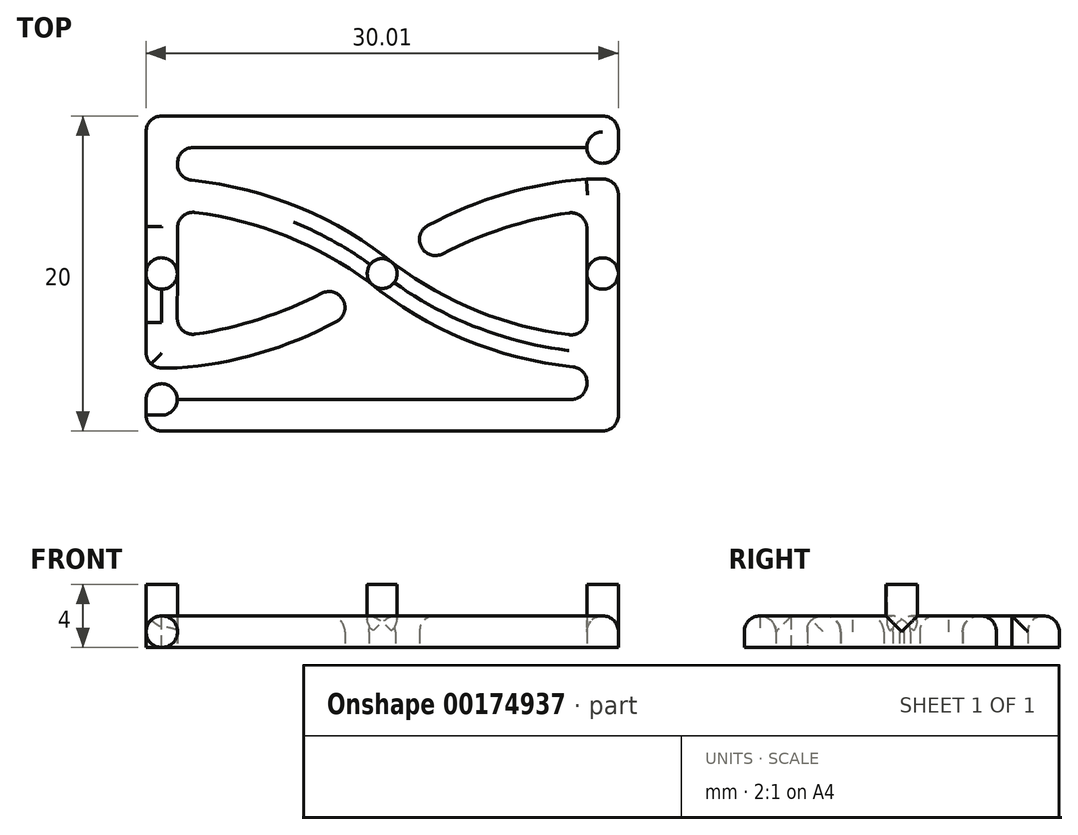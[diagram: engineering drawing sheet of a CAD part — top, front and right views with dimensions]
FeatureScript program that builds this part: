
annotation { "Feature Type Name" : "Feature", "Feature Type Description" : "" }
export const myFeature = defineFeature(function(context is Context, id is Id, definition is map)
    precondition{}
    {
        {
            var Q0;
            Q0=qCreatedBy(makeId("Top.planeOp"),FACE);
            var sketch = newSketch(context, id + "F0", { "sketchPlane" : qUnion([Q0])});
            skLineSegment(sketch, "E0", {"start": v(-15, 10) * mm, "end": v(-15, -6) * mm, "construction": true});
            skLineSegment(sketch, "E1", {"start": v(-15, -10) * mm, "end": v(15, -10) * mm, "construction": true});
            skLineSegment(sketch, "E2", {"start": v(15, -10) * mm, "end": v(15, 6.02) * mm, "construction": true});
            skLineSegment(sketch, "E3", {"start": v(15, 10) * mm, "end": v(-15, 10) * mm, "construction": true});
            skLineSegment(sketch, "E4", {"start": v(-15, 10) * mm, "end": v(15, 10) * mm});
            skLineSegment(sketch, "E5", {"start": v(15, 7) * mm, "end": v(13, 7) * mm});
            skLineSegment(sketch, "E6", {"start": v(13, 7) * mm, "end": v(13, 8) * mm});
            skLineSegment(sketch, "E7", {"start": v(13, 8) * mm, "end": v(-13, 8) * mm});
            skLineSegment(sketch, "E8", {"start": v(-13, 8) * mm, "end": v(-13, 6) * mm});
            skLineSegment(sketch, "E9", {"start": v(-15, 10) * mm, "end": v(-15, -7.49) * mm});
            skLineSegment(sketch, "E10", {"start": v(-15, -10) * mm, "end": v(-15, -7) * mm});
            skLineSegment(sketch, "E11", {"start": v(-15, -7) * mm, "end": v(-13.02, -7) * mm});
            skLineSegment(sketch, "E12", {"start": v(-13.02, -7) * mm, "end": v(-13.02, -8) * mm});
            skLineSegment(sketch, "E13", {"start": v(-13.02, -8) * mm, "end": v(13, -8) * mm});
            skLineSegment(sketch, "E14", {"start": v(13, -8) * mm, "end": v(13, -6) * mm});
            skLineSegment(sketch, "E15", {"start": v(-15, -7) * mm, "end": v(-15, -10) * mm});
            skLineSegment(sketch, "E16", {"start": v(15, -10) * mm, "end": v(-15, -10) * mm});
            skLineSegment(sketch, "E17", {"start": v(15, -10) * mm, "end": v(15, 7) * mm});
            skLineSegment(sketch, "E18", {"start": v(15, 10) * mm, "end": v(-15, -10) * mm, "construction": true});
            skLineSegment(sketch, "E19", {"start": v(-15, 10) * mm, "end": v(15, -10) * mm, "construction": true});
            skPoint(sketch, "E20", {"position": v(0, 0) * mm});
            skLineSegment(sketch, "E21", {"start": v(0, 0) * mm, "end": v(0.83, -0.55) * mm});
            skArc(sketch, "E22", {"start": v(0.83, 0.55) * mm, "mid": v(-5.66, 4.36) * mm, "end": v(-13, 6) * mm});
            skPoint(sketch, "E23", {"position": v(13, -4) * mm});
            skPoint(sketch, "E24", {"position": v(-13, 6) * mm});
            skPoint(sketch, "E25", {"position": v(-13, 4) * mm});
            skArc(sketch, "E26", {"start": v(-0.83, -0.55) * mm, "mid": v(-6.6, 2.57) * mm, "end": v(-13, 4) * mm});
            skArc(sketch, "E27", {"start": v(-0.83, -0.55) * mm, "mid": v(5.66, -4.35) * mm, "end": v(13, -6) * mm});
            skArc(sketch, "E28", {"start": v(0.83, 0.55) * mm, "mid": v(6.6, -2.59) * mm, "end": v(13, -4) * mm});
            skPoint(sketch, "E29", {"position": v(13, 6) * mm});
            skPoint(sketch, "E30", {"position": v(-13.02, -6) * mm});
            skPoint(sketch, "E31", {"position": v(2.5, 1.66) * mm});
            skPoint(sketch, "E32", {"position": v(-2.5, -1.66) * mm});
            skLineSegment(sketch, "E33", {"start": v(-2.5, -1.66) * mm, "end": v(-3.05, -0.83) * mm, "construction": true});
            skLineSegment(sketch, "E34", {"start": v(-2.5, -1.66) * mm, "end": v(-1.94, -2.5) * mm, "construction": true});
            skLineSegment(sketch, "E35", {"start": v(2.5, 1.66) * mm, "end": v(3.05, 0.83) * mm, "construction": true});
            skLineSegment(sketch, "E36", {"start": v(3.05, 0.83) * mm, "end": v(1.94, 2.5) * mm, "construction": true});
            skLineSegment(sketch, "E37", {"start": v(15, 6.02) * mm, "end": v(13, 6) * mm});
            skPoint(sketch, "E38", {"position": v(-13.02, -4) * mm});
            skLineSegment(sketch, "E39", {"start": v(-13.02, -6) * mm, "end": v(-15, -6) * mm});
            skArc(sketch, "E40", {"start": v(-13.02, -6) * mm, "mid": v(-7.27, -4.9) * mm, "end": v(-1.94, -2.5) * mm});
            skArc(sketch, "E41", {"start": v(-13.02, -4) * mm, "mid": v(-7.88, -2.92) * mm, "end": v(-3.05, -0.83) * mm});
            skLineSegment(sketch, "E42", {"start": v(-3.05, -0.83) * mm, "end": v(-1.94, -2.5) * mm});
            skLineSegment(sketch, "E43", {"start": v(-13.02, -4) * mm, "end": v(-13, 4) * mm});
            skArc(sketch, "E44", {"start": v(13, 6) * mm, "mid": v(7.26, 4.9) * mm, "end": v(1.94, 2.5) * mm});
            skPoint(sketch, "E45", {"position": v(13, 4) * mm});
            skArc(sketch, "E46", {"start": v(13, 4) * mm, "mid": v(7.87, 2.92) * mm, "end": v(3.05, 0.83) * mm});
            skLineSegment(sketch, "E47", {"start": v(13, 4) * mm, "end": v(13, -4) * mm});
            skLineSegment(sketch, "E48", {"start": v(3.05, 0.83) * mm, "end": v(1.94, 2.5) * mm});
            skLineSegment(sketch, "E49", {"start": v(15, 6.02) * mm, "end": v(15, -10) * mm});
            skLineSegment(sketch, "E50", {"start": v(15, 7) * mm, "end": v(15, 10) * mm});
            skLineSegment(sketch, "E51.trimOffspring", {"start": v(15, 7) * mm, "end": v(15, 10) * mm, "construction": true});
            skLineSegment(sketch, "E52.trimOffspring", {"start": v(-15, -7) * mm, "end": v(-15, -10) * mm, "construction": true});
            skSolve(sketch);
        }
        {
            var Q0;
            {var subQ5=sQuery(id+"F0.wireOp",EDGE,"E4");Q0=makeQuery(id+"F0.imprint","IMPRINT",FACE,{"disambiguationData":[TD([[makeQuery(id+"F0.imprint","IMPRINT",EDGE,{"derivedFrom":subQ5}),-1.0]])]});}
            extrude(context, id + "F1", {"entities" : qUnion([Q0]), "depth" : 2 * mm});
        }
        {
            var Q0;
            Q0=makeQuery(id+"F1.opExtrude","SWEPT_EDGE",EDGE,{"disambiguationData":[OSD([sQuery(id+"F0.wireOp",EDGE,"E44"),sQuery(id+"F0.wireOp",EDGE,"E48")])]});
            var Q1;
            Q1=makeQuery(id+"F1.opExtrude","SWEPT_EDGE",EDGE,{"disambiguationData":[OSD([sQuery(id+"F0.wireOp",EDGE,"E46"),sQuery(id+"F0.wireOp",EDGE,"E48")])]});
            var Q2;
            Q2=makeQuery(id+"F1.opExtrude","SWEPT_EDGE",EDGE,{"disambiguationData":[OSD([sQuery(id+"F0.wireOp",EDGE,"E5"),sQuery(id+"F0.wireOp",EDGE,"E6")])]});
            var Q3;
            Q3=makeQuery(id+"F1.opExtrude","SWEPT_EDGE",EDGE,{"disambiguationData":[OSD([sQuery(id+"F0.wireOp",EDGE,"E5"),sQuery(id+"F0.wireOp",EDGE,"E17"),sQuery(id+"F0.wireOp",EDGE,"E50")])]});
            var Q4;
            Q4=makeQuery(id+"F1.opExtrude","SWEPT_EDGE",EDGE,{"disambiguationData":[OSD([sQuery(id+"F0.wireOp",EDGE,"E9"),sQuery(id+"F0.wireOp",EDGE,"E39")])]});
            var Q5;
            Q5=makeQuery(id+"F1.opExtrude","SWEPT_EDGE",EDGE,{"disambiguationData":[OSD([sQuery(id+"F0.wireOp",EDGE,"E9"),sQuery(id+"F0.wireOp",EDGE,"E11"),sQuery(id+"F0.wireOp",EDGE,"E15")])]});
            var Q6;
            Q6=makeQuery(id+"F1.opExtrude","SWEPT_EDGE",EDGE,{"disambiguationData":[OSD([sQuery(id+"F0.wireOp",EDGE,"E15"),sQuery(id+"F0.wireOp",EDGE,"E16")])]});
            var Q7;
            Q7=makeQuery(id+"F1.opExtrude","SWEPT_EDGE",EDGE,{"disambiguationData":[OSD([sQuery(id+"F0.wireOp",EDGE,"E46"),sQuery(id+"F0.wireOp",EDGE,"E47")])]});
            var Q8;
            Q8=makeQuery(id+"F1.opExtrude","SWEPT_EDGE",EDGE,{"disambiguationData":[OSD([sQuery(id+"F0.wireOp",EDGE,"E14"),sQuery(id+"F0.wireOp",EDGE,"E27")])]});
            var Q9;
            Q9=makeQuery(id+"F1.opExtrude","SWEPT_EDGE",EDGE,{"disambiguationData":[OSD([sQuery(id+"F0.wireOp",EDGE,"E16"),sQuery(id+"F0.wireOp",EDGE,"E49")])]});
            var Q10;
            Q10=makeQuery(id+"F1.opExtrude","SWEPT_EDGE",EDGE,{"disambiguationData":[OSD([sQuery(id+"F0.wireOp",EDGE,"E7"),sQuery(id+"F0.wireOp",EDGE,"E8")])]});
            var Q11;
            Q11=makeQuery(id+"F1.opExtrude","SWEPT_EDGE",EDGE,{"disambiguationData":[OSD([sQuery(id+"F0.wireOp",EDGE,"E26"),sQuery(id+"F0.wireOp",EDGE,"E43")])]});
            var Q12;
            Q12=makeQuery(id+"F1.opExtrude","SWEPT_EDGE",EDGE,{"disambiguationData":[OSD([sQuery(id+"F0.wireOp",EDGE,"E40"),sQuery(id+"F0.wireOp",EDGE,"E42")])]});
            var Q13;
            Q13=makeQuery(id+"F1.opExtrude","SWEPT_EDGE",EDGE,{"disambiguationData":[OSD([sQuery(id+"F0.wireOp",EDGE,"E4"),sQuery(id+"F0.wireOp",EDGE,"E50")])]});
            var Q14;
            Q14=makeQuery(id+"F1.opExtrude","SWEPT_EDGE",EDGE,{"disambiguationData":[OSD([sQuery(id+"F0.wireOp",EDGE,"E13"),sQuery(id+"F0.wireOp",EDGE,"E14")])]});
            var Q15;
            Q15=makeQuery(id+"F1.opExtrude","SWEPT_EDGE",EDGE,{"disambiguationData":[OSD([sQuery(id+"F0.wireOp",EDGE,"E28"),sQuery(id+"F0.wireOp",EDGE,"E47")])]});
            var Q16;
            Q16=makeQuery(id+"F1.opExtrude","SWEPT_EDGE",EDGE,{"disambiguationData":[OSD([sQuery(id+"F0.wireOp",EDGE,"E4"),sQuery(id+"F0.wireOp",EDGE,"E9")])]});
            var Q17;
            Q17=makeQuery(id+"F1.opExtrude","SWEPT_EDGE",EDGE,{"disambiguationData":[OSD([sQuery(id+"F0.wireOp",EDGE,"E41"),sQuery(id+"F0.wireOp",EDGE,"E43")])]});
            var Q18;
            Q18=makeQuery(id+"F1.opExtrude","SWEPT_EDGE",EDGE,{"disambiguationData":[OSD([sQuery(id+"F0.wireOp",EDGE,"E8"),sQuery(id+"F0.wireOp",EDGE,"E22")])]});
            var Q19;
            Q19=makeQuery(id+"F1.opExtrude","SWEPT_EDGE",EDGE,{"disambiguationData":[OSD([sQuery(id+"F0.wireOp",EDGE,"E41"),sQuery(id+"F0.wireOp",EDGE,"E42")])]});
            var Q20;
            Q20=makeQuery(id+"F1.opExtrude","SWEPT_EDGE",EDGE,{"disambiguationData":[OSD([sQuery(id+"F0.wireOp",EDGE,"E11"),sQuery(id+"F0.wireOp",EDGE,"E12")])]});
            var Q21;
            Q21=makeQuery(id+"F1.opExtrude","SWEPT_EDGE",EDGE,{"disambiguationData":[OSD([sQuery(id+"F0.wireOp",EDGE,"E17"),sQuery(id+"F0.wireOp",EDGE,"E37"),sQuery(id+"F0.wireOp",EDGE,"E49")])]});
            fillet(context, id + "F2", {"entities" : qUnion([Q0, Q1, Q2, Q3, Q4, Q5, Q6, Q7, Q8, Q9, Q10, Q11, Q12, Q13, Q14, Q15, Q16, Q17, Q18, Q19, Q20, Q21]), "radius" : 1 * mm, "tangentPropagation" : true, "allowEdgeOverflow" : false});
        }
        {
            var Q0;
            Q0=makeQuery(id+"F1.opExtrude","CAP_EDGE",EDGE,{"disambiguationData":[OSD([sQuery(id+"F0.wireOp",EDGE,"E27")])],"isStart":false});
            var Q1;
            Q1=makeQuery(id+"F1.opExtrude","CAP_EDGE",EDGE,{"disambiguationData":[OSD([sQuery(id+"F0.wireOp",EDGE,"E40")])],"isStart":false});
            var Q2;
            Q2=makeQuery(id+"F1.opExtrude","CAP_EDGE",EDGE,{"disambiguationData":[OSD([sQuery(id+"F0.wireOp",EDGE,"E46")])],"isStart":false});
            var Q3;
            Q3=makeQuery(id+"F1.opExtrude","CAP_EDGE",EDGE,{"disambiguationData":[OSD([sQuery(id+"F0.wireOp",EDGE,"E7")])],"isStart":false});
            fillet(context, id + "F3", {"entities" : qUnion([Q0, Q1, Q2, Q3]), "radius" : 1 * mm, "tangentPropagation" : true, "allowEdgeOverflow" : false});
        }
        {
            var Q0;
            Q0=makeQuery(id+"F1.opExtrude","CAP_EDGE",EDGE,{"disambiguationData":[OSD([sQuery(id+"F0.wireOp",EDGE,"E16")])],"isStart":false});
            fillet(context, id + "F4", {"entities" : qUnion([Q0]), "radius" : 1 * mm, "tangentPropagation" : true, "allowEdgeOverflow" : false});
        }
        {
            var Q0;
            Q0=makeQuery(id+"F1.opExtrude","CAP_EDGE",EDGE,{"disambiguationData":[OSD([sQuery(id+"F0.wireOp",EDGE,"E4")])],"isStart":false});
            var Q1;
            Q1=makeQuery(id+"F1.opExtrude","CAP_EDGE",EDGE,{"disambiguationData":[OSD([sQuery(id+"F0.wireOp",EDGE,"E9")])],"isStart":false});
            var Q2;
            Q2=makeQuery(id+"F1.opExtrude","CAP_EDGE",EDGE,{"disambiguationData":[OSD([sQuery(id+"F0.wireOp",EDGE,"E50")])],"isStart":false});
            fillet(context, id + "F5", {"entities" : qUnion([Q0, Q1, Q2]), "radius" : 1 * mm, "allowEdgeOverflow" : false});
        }
        {
            var Q0;
            Q0=qCreatedBy(makeId("Top.planeOp"),FACE);
            var sketch = newSketch(context, id + "F6", { "sketchPlane" : qUnion([Q0])});
            skCircle(sketch, "E53", {"center": v(-14, 0) * mm, "radius": 1 * mm});
            skCircle(sketch, "E54", {"center": v(0, 0) * mm, "radius": 0.95 * mm});
            skCircle(sketch, "E55", {"center": v(14, 0) * mm, "radius": 1 * mm});
            skSolve(sketch);
        }
        {
            var Q0;
            Q0 = qSketchRegion(id + "F6", true);
            extrude(context, id + "F7", {"entities" : qUnion([Q0]), "operationType" : NewBodyOperationType.ADD, "depth" : 4 * mm});
        }
    });
